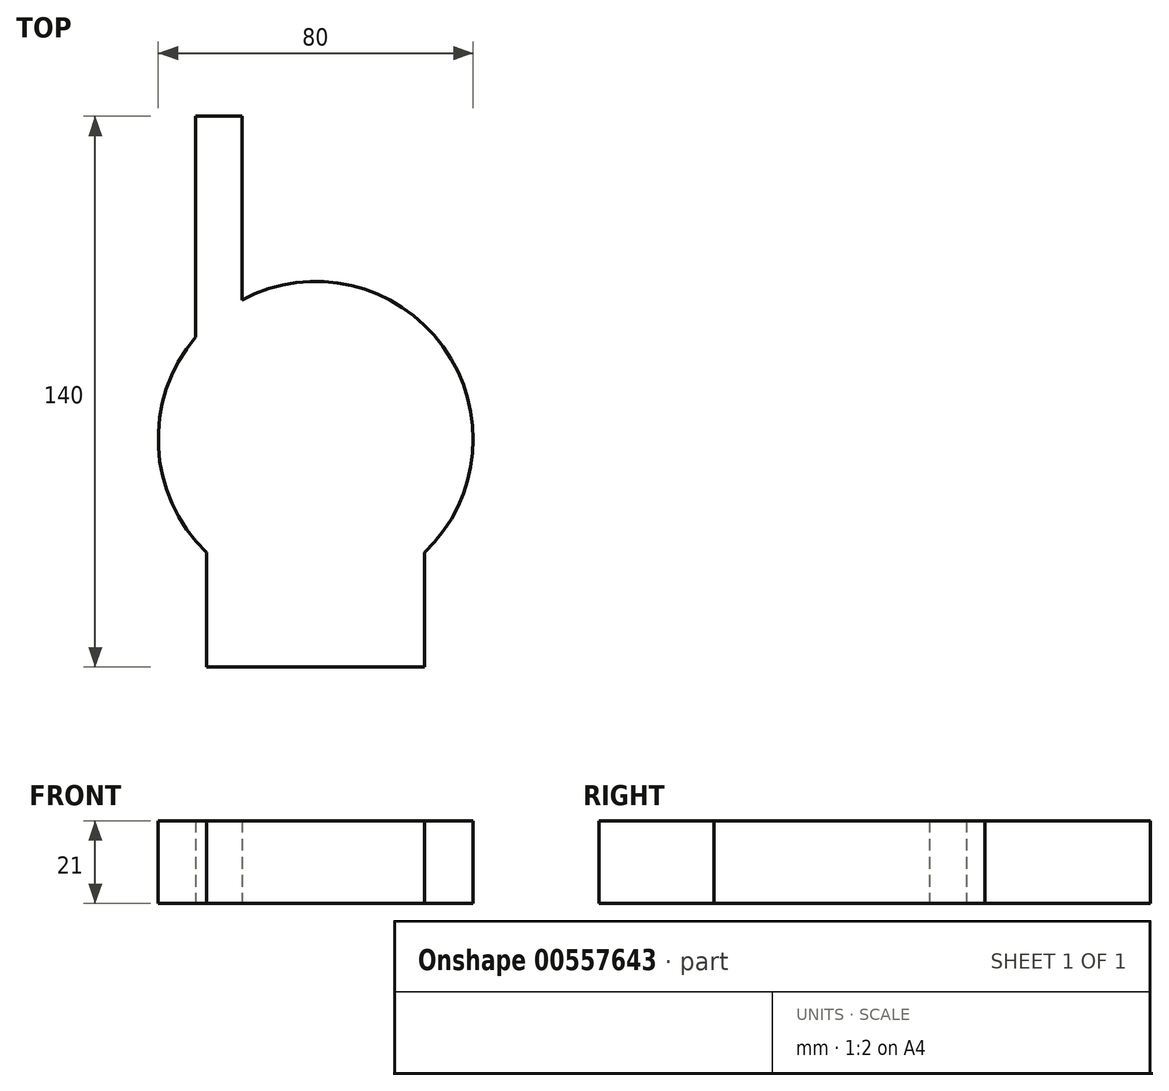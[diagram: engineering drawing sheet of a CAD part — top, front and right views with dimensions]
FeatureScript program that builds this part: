
annotation { "Feature Type Name" : "Feature", "Feature Type Description" : "" }
export const myFeature = defineFeature(function(context is Context, id is Id, definition is map)
    precondition{}
    {
        {
            var Q0;
            Q0=qCreatedBy(makeId("Top.planeOp"),FACE);
            var sketch = newSketch(context, id + "F0", { "sketchPlane" : qUnion([Q0])});
            skArc(sketch, "E0", {"start": v(27.69, -28.87) * mm, "mid": v(32.42, 23.43) * mm, "end": v(-18.73, 35.34) * mm});
            skLineSegment(sketch, "E1", {"start": v(-27.69, -28.87) * mm, "end": v(-27.69, -58) * mm});
            skLineSegment(sketch, "E2", {"start": v(-27.69, -58) * mm, "end": v(27.69, -58) * mm});
            skLineSegment(sketch, "E3", {"start": v(27.69, -58) * mm, "end": v(27.69, -28.87) * mm});
            skLineSegment(sketch, "E4", {"start": v(-30.45, 25.93) * mm, "end": v(-30.45, 82) * mm});
            skLineSegment(sketch, "E5", {"start": v(-30.45, 82) * mm, "end": v(-18.73, 82) * mm});
            skLineSegment(sketch, "E6", {"start": v(-18.73, 82) * mm, "end": v(-18.73, 35.34) * mm});
            skArc(sketch, "E7.trimOffspring", {"start": v(-30.45, 25.93) * mm, "mid": v(-39.95, -2.02) * mm, "end": v(-27.69, -28.87) * mm});
            skSolve(sketch);
        }
        {
            var Q0;
            Q0=makeQuery(id+"F0.imprint","IMPRINT",FACE,{"disambiguationData":[TD([[makeQuery(id+"F0.imprint","IMPRINT",EDGE,{"derivedFrom":sQuery(id+"F0.wireOp",EDGE,"E0")}),1.0]])]});
            extrude(context, id + "F1", {"entities" : qUnion([Q0]), "depth" : 21 * mm, "offsetDistance" : 25 * mm});
        }
    });
